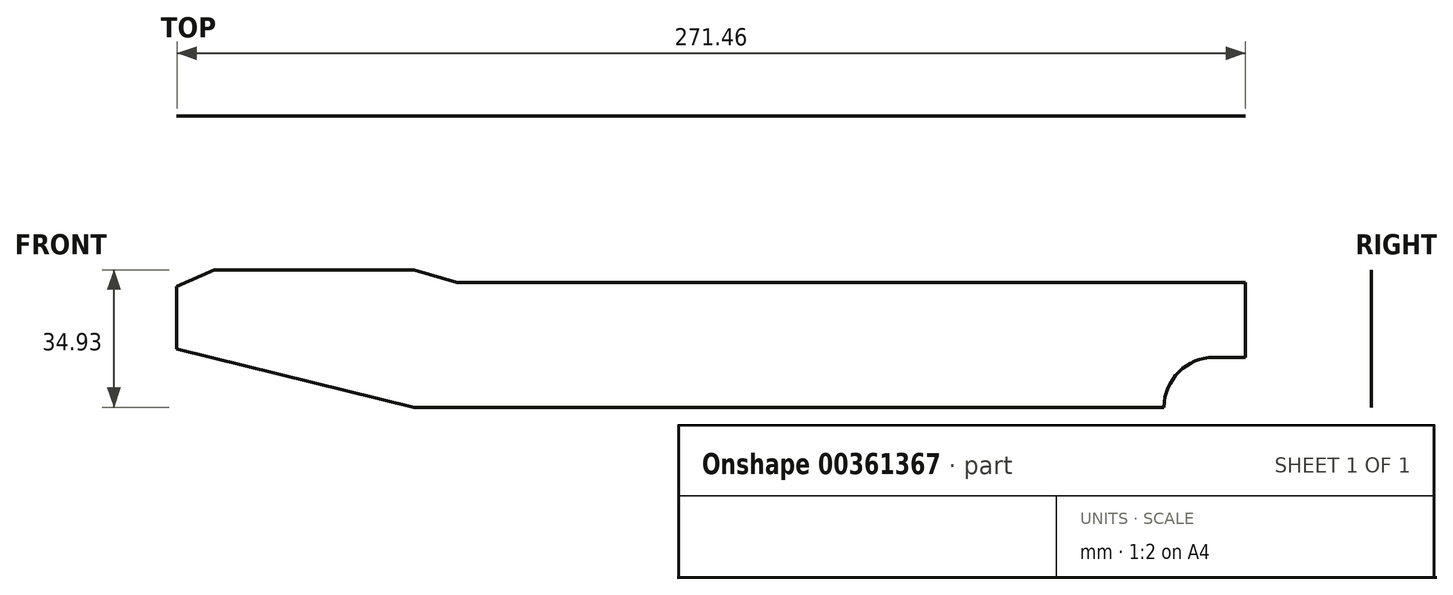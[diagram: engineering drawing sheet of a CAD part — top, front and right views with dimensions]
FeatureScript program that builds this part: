
annotation { "Feature Type Name" : "Feature", "Feature Type Description" : "" }
export const myFeature = defineFeature(function(context is Context, id is Id, definition is map)
    precondition{}
    {
        {
            var Q0;
            Q0=qCreatedBy(makeId("Front.planeOp"),FACE);
            var sketch = newSketch(context, id + "F0", { "sketchPlane" : qUnion([Q0])});
            skLineSegment(sketch, "E0", {"start": v(-100.5, 0.48) * mm, "end": v(-40.17, -14.3) * mm});
            skLineSegment(sketch, "E1", {"start": v(-40.17, -14.3) * mm, "end": v(150.33, -14.3) * mm});
            skLineSegment(sketch, "E2", {"start": v(150.33, -14.3) * mm, "end": v(150.33, -14.3) * mm});
            skLineSegment(sketch, "E3", {"start": v(163.03, -1.6) * mm, "end": v(170.97, -1.6) * mm});
            skLineSegment(sketch, "E4", {"start": v(170.97, -1.6) * mm, "end": v(170.97, 17.44) * mm});
            skLineSegment(sketch, "E5", {"start": v(170.97, 17.44) * mm, "end": v(-29.3, 17.44) * mm});
            skLineSegment(sketch, "E6", {"start": v(-29.3, 17.44) * mm, "end": v(-40.17, 20.62) * mm});
            skLineSegment(sketch, "E7", {"start": v(-40.17, 20.62) * mm, "end": v(-90.97, 20.62) * mm});
            skLineSegment(sketch, "E8", {"start": v(-100.5, 0.48) * mm, "end": v(-100.5, 16.35) * mm});
            skLineSegment(sketch, "E9", {"start": v(-40.17, 8.54) * mm, "end": v(-40.17, -75.17) * mm, "construction": true});
            skLineSegment(sketch, "E10", {"start": v(-100.5, 16.35) * mm, "end": v(-90.97, 20.62) * mm});
            skLineSegment(sketch, "E11", {"start": v(-90.97, 60.97) * mm, "end": v(-90.97, -18.8) * mm, "construction": true});
            skPoint(sketch, "E12.visualSharp", {"position": v(150.33, -1.6) * mm});
            skArc(sketch, "E12.filletArc", {"start": v(163.03, -1.6) * mm, "mid": v(154.05, -5.33) * mm, "end": v(150.33, -14.3) * mm});
            skSolve(sketch);
        }
        {
            var Q0;
            Q0=makeQuery(id+"F0.imprint","IMPRINT",FACE,{"disambiguationData":[TD([[makeQuery(id+"F0.imprint","IMPRINT",EDGE,{"derivedFrom":sQuery(id+"F0.wireOp",EDGE,"E0")}),1.0]])]});
            extrude(context, id + "F1", {"entities" : qUnion([Q0]), "depth" : 1 / 406.4 * mm});
        }
    });
